# Revit family: KingswayGroup_TltPprDspnsrs_Anti-LigatureToiletTissueDispenserRecessed
name_source: partatom
category: Specialty Equipment
units: mm (PartAtom-declared; Revit-internal decimal feet)

## family parameters
Always vertical = Yes
Cut with Voids When Loaded = No
Part Type = Normal
Room Calculation Point = No
Round Connector Dimension = Use Diameter
Shared = No
Work Plane-Based = No

## types (1)
- KingswayGroup_TltPprDspnsrs_Anti-LigatureToiletTissueDispenserRecessed
    AssetType = Fixed
    BIMObjectName = KingswayGroup_ToiletPaperDispensers_Anti-LigatureToiletTissueDispenserRecessed
    Category = Pr_40_70_22_90:Toilet paper dispensers
    Color = For full range of available finishes and colours, contact Kingsway Group
    Default Elevation = 0 mm  [stored 0 ft]
    Description = Recessed Toilet Tissue Dispenser
    DispenserMaterial = NBS_Concept
    DurationUnit = year
    Features = A recessed Anti-Ligature Toilet Tissue dispenser to improve service user safety in mental health facility washrooms. The KG10 Anti-Ligature Toilet Tissue Dispenser is fitted flush with the wall to provide a well styled yet robust solution that offers exceptional durability and corrosion resistance.
    Finish = For full range of available finishes and colours, contact Kingsway Group
    Grade = 316
    Manufacturer = Kingsway Group
    ManufacturerName = Kingsway Group
    ManufacturerURL = https://kingswaygroupglobal.com
    Material = Stainless Steel
    Model = KG10
    ModelNumber = KG10
    ModelReference = Anti-Ligature Toilet Tissue Dispenser (Recessed)
    Name = ToiletPaperDispensers_Anti-LigatureToiletTissueDispenserRecessed_KG10_KingswayGroup
    NominalHeight = 394 mm
    NominalLength = 191 mm  [stored 0.62664 ft]
    NominalWidth = 106 mm  [stored 0.347769 ft]
    ProductInformation = https://kingswaygroupglobal.com
    Size = 191 x 394 x 106 mm
    URL = https://kingswaygroupglobal.com
    Uniclass2015Code = Pr_40_70_22_90
    Uniclass2015Title = Toilet paper dispensers
    Uniclass2015Version = Products v1.36
    Version = 1
    WarrantyDescription = 5-Year Guarantee *For faulty manufacture and not for damage
    WarrantyDurationParts = 5
    WarrantyDurationUnit = year

note: [stored X ft] marks values corroborated as IEEE doubles in the binary element streams (Revit-internal decimal feet)

## geometry (parser evidence)
native form markers: Sweep x2
no freeform markers — native parametric forms only
